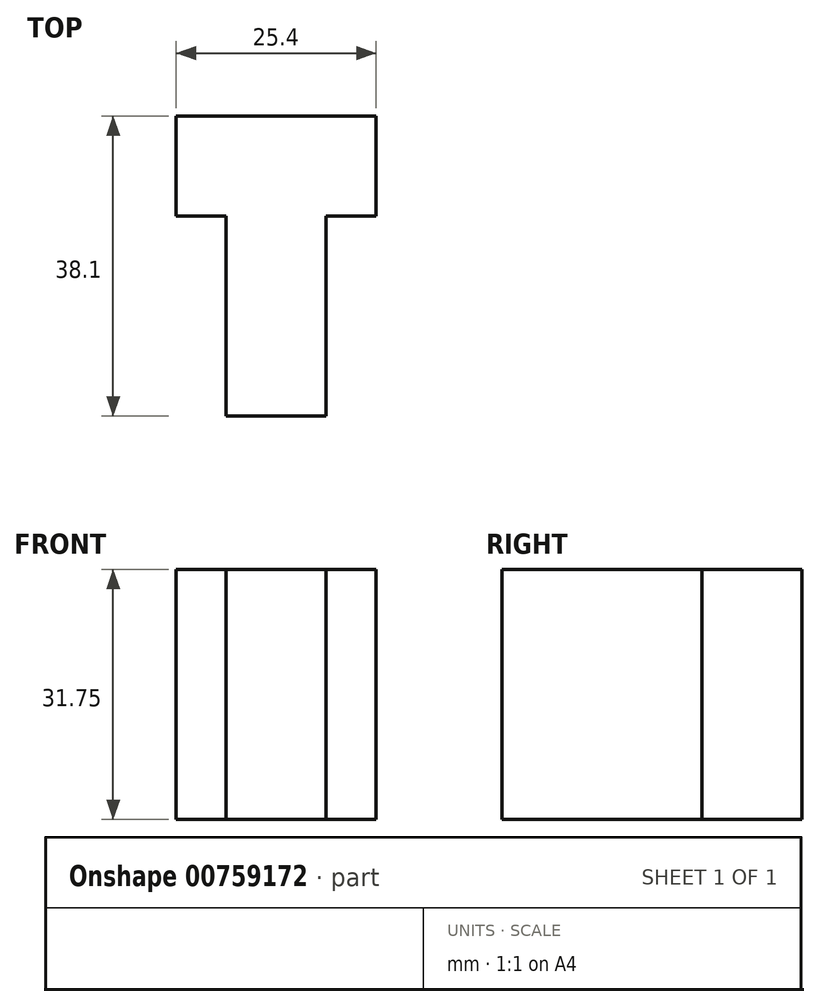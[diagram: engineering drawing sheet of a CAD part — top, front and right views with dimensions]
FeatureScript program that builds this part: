
annotation { "Feature Type Name" : "Feature", "Feature Type Description" : "" }
export const myFeature = defineFeature(function(context is Context, id is Id, definition is map)
    precondition{}
    {
        {
            var Q0;
            Q0=qCreatedBy(makeId("Top.planeOp"),FACE);
            var sketch = newSketch(context, id + "F0", { "sketchPlane" : qUnion([Q0])});
            skLineSegment(sketch, "E0", {"start": v(0, 0) * mm, "end": v(-6.35, 0) * mm});
            skLineSegment(sketch, "E1", {"start": v(-6.35, 0) * mm, "end": v(-6.35, 12.7) * mm});
            skLineSegment(sketch, "E2", {"start": v(-6.35, 12.7) * mm, "end": v(19.05, 12.7) * mm});
            skLineSegment(sketch, "E3", {"start": v(19.05, 12.7) * mm, "end": v(19.05, 0) * mm});
            skLineSegment(sketch, "E4", {"start": v(19.05, 0) * mm, "end": v(12.7, 0) * mm});
            skLineSegment(sketch, "E5", {"start": v(12.7, 0) * mm, "end": v(12.7, -25.4) * mm});
            skLineSegment(sketch, "E6", {"start": v(12.7, -25.4) * mm, "end": v(0, -25.4) * mm});
            skLineSegment(sketch, "E7", {"start": v(0, -25.4) * mm, "end": v(0, 0) * mm});
            skSolve(sketch);
        }
        {
            var Q0;
            Q0=makeQuery(id+"F0.imprint","IMPRINT",FACE,{"disambiguationData":[TD([[makeQuery(id+"F0.imprint","IMPRINT",EDGE,{"derivedFrom":sQuery(id+"F0.wireOp",EDGE,"E0")}),-1.0]])]});
            extrude(context, id + "F1", {"entities" : qUnion([Q0]), "depth" : 31.75 * mm, "offsetDistance" : 25.4 * mm});
        }
    });
